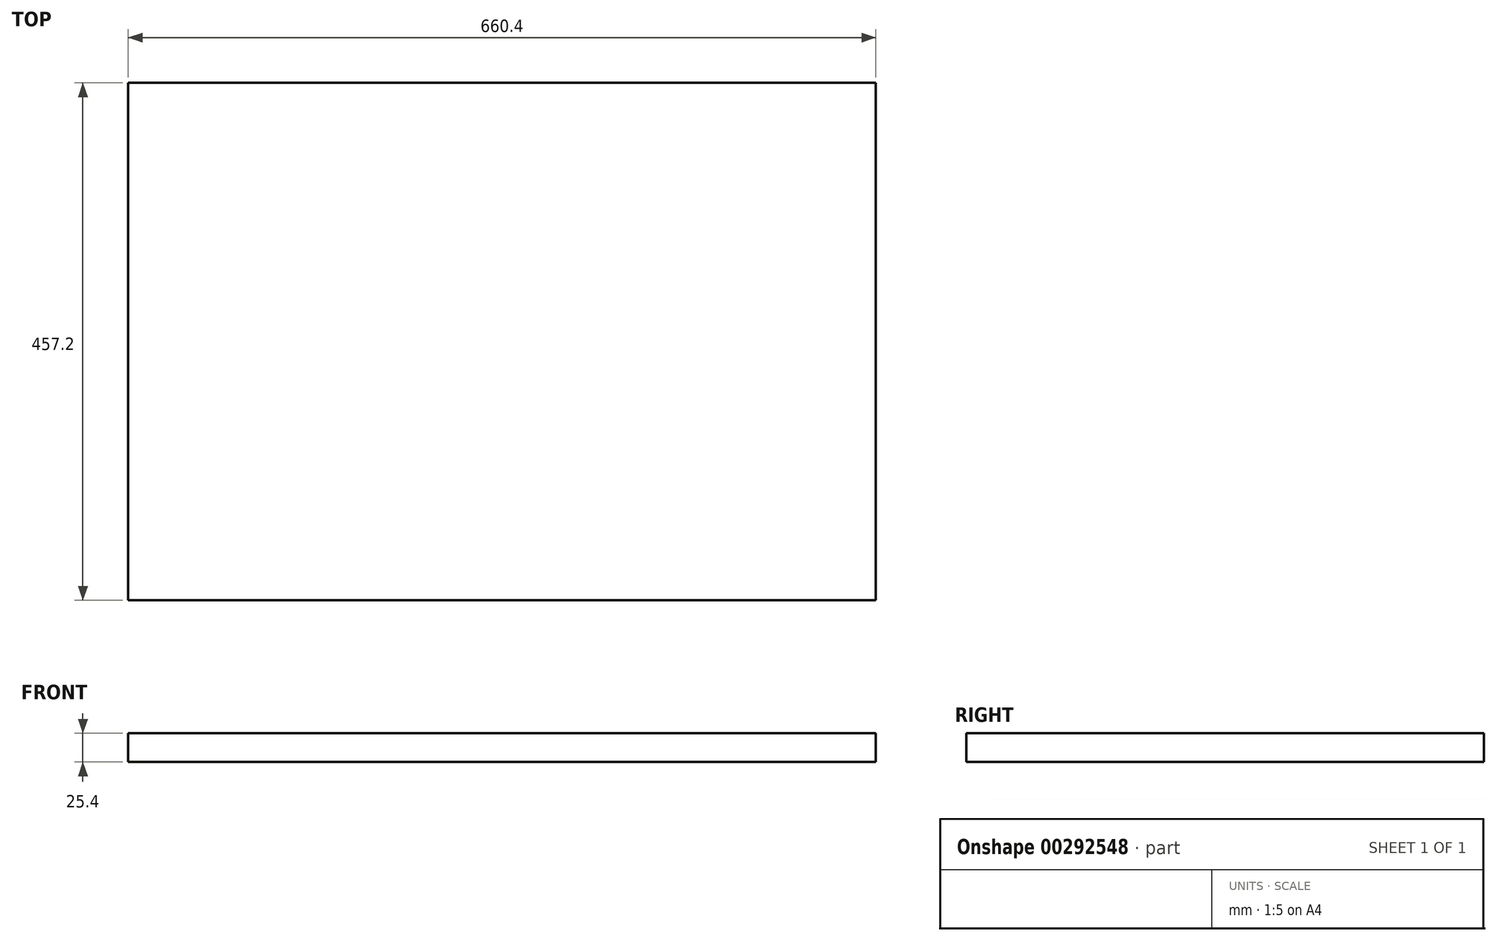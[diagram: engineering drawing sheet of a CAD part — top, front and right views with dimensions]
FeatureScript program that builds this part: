
annotation { "Feature Type Name" : "Feature", "Feature Type Description" : "" }
export const myFeature = defineFeature(function(context is Context, id is Id, definition is map)
    precondition{}
    {
        {
            var Q0;
            Q0=qCreatedBy(makeId("Top.planeOp"),FACE);
            var sketch = newSketch(context, id + "F0", { "sketchPlane" : qUnion([Q0])});
            skLineSegment(sketch, "E0.bottom", {"start": v(0, 0) * mm, "end": v(660.4, 0) * mm});
            skLineSegment(sketch, "E0.top", {"start": v(0, 457.2) * mm, "end": v(660.4, 457.2) * mm});
            skLineSegment(sketch, "E0.left", {"start": v(0, 0) * mm, "end": v(0, 457.2) * mm});
            skLineSegment(sketch, "E0.right", {"start": v(660.4, 0) * mm, "end": v(660.4, 457.2) * mm});
            skSolve(sketch);
        }
        {
            var Q0;
            Q0 = qSketchRegion(id + "F0", true);
            extrude(context, id + "F1", {"entities" : qUnion([Q0]), "depth" : 25.4 * mm});
        }
    });
